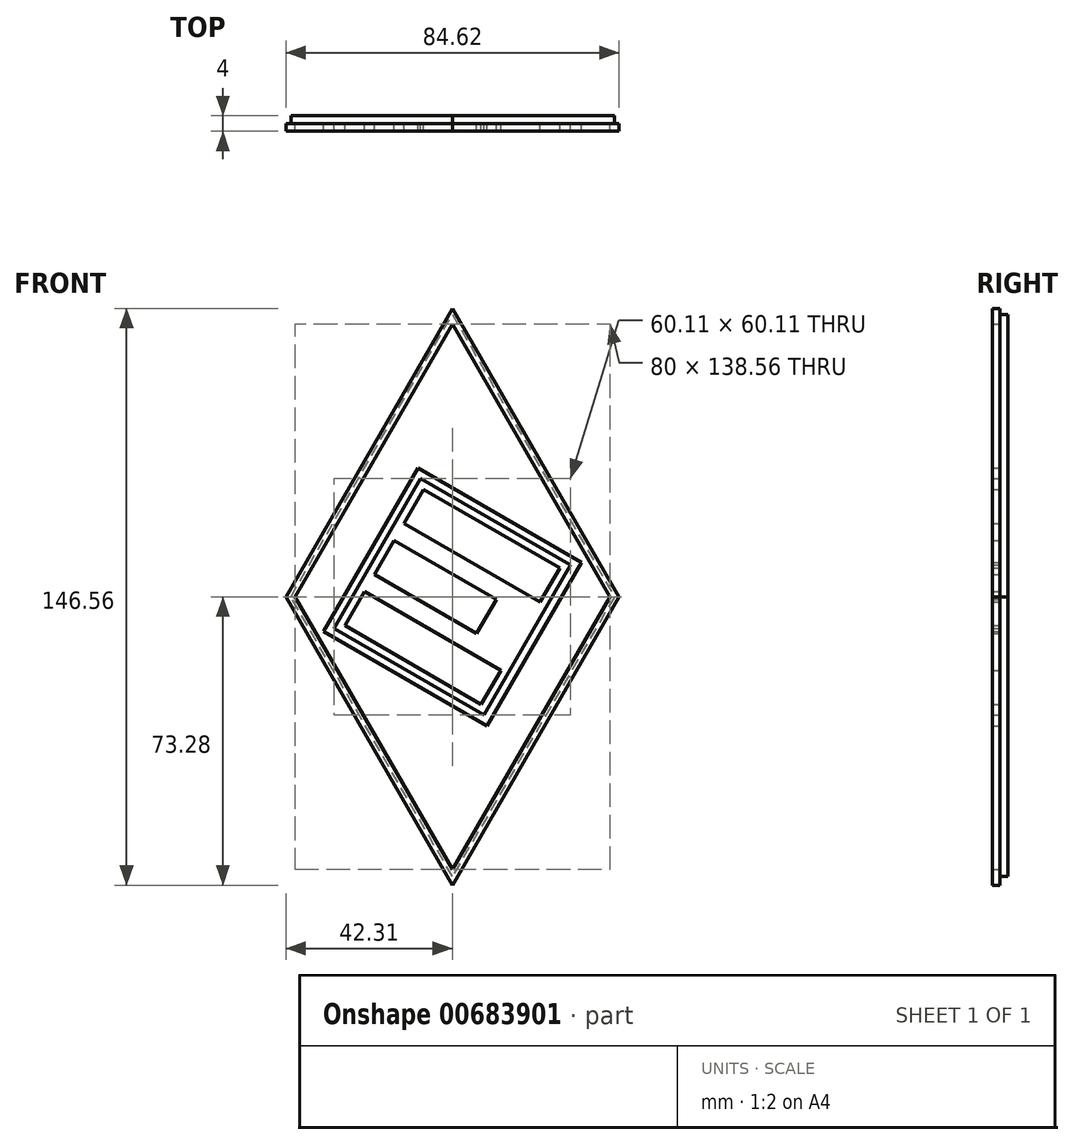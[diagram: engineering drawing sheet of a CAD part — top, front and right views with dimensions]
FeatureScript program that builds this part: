
annotation { "Feature Type Name" : "Feature", "Feature Type Description" : "" }
export const myFeature = defineFeature(function(context is Context, id is Id, definition is map)
    precondition{}
    {
        {
            var Q0;
            Q0=qCreatedBy(makeId("Front.planeOp"),FACE);
            var sketch = newSketch(context, id + "F0", { "sketchPlane" : qUnion([Q0])});
            skLineSegment(sketch, "E0.bottom", {"start": v(7.32, -27.32) * mm, "end": v(-27.32, -7.32) * mm});
            skLineSegment(sketch, "E0.top", {"start": v(12.32, -18.66) * mm, "end": v(-22.32, 1.34) * mm});
            skLineSegment(sketch, "E0.left", {"start": v(7.32, -27.32) * mm, "end": v(12.32, -18.66) * mm});
            skLineSegment(sketch, "E0.right", {"start": v(-27.32, -7.32) * mm, "end": v(-22.32, 1.34) * mm});
            skLineSegment(sketch, "E1.bottom", {"start": v(-14.82, 14.33) * mm, "end": v(11.16, -0.67) * mm});
            skLineSegment(sketch, "E1.top", {"start": v(-19.82, 5.67) * mm, "end": v(6.16, -9.33) * mm});
            skLineSegment(sketch, "E1.left", {"start": v(-14.82, 14.33) * mm, "end": v(-19.82, 5.67) * mm});
            skLineSegment(sketch, "E1.right", {"start": v(11.16, -0.67) * mm, "end": v(6.16, -9.33) * mm});
            skLineSegment(sketch, "E2.bottom", {"start": v(-12.32, 18.66) * mm, "end": v(22.32, -1.34) * mm});
            skLineSegment(sketch, "E2.top", {"start": v(-7.32, 27.32) * mm, "end": v(27.32, 7.32) * mm});
            skLineSegment(sketch, "E2.left", {"start": v(-12.32, 18.66) * mm, "end": v(-7.32, 27.32) * mm});
            skLineSegment(sketch, "E2.right", {"start": v(22.32, -1.34) * mm, "end": v(27.32, 7.32) * mm});
            skLineSegment(sketch, "E3.0", {"start": v(-22.32, 1.34) * mm, "end": v(-22.32, 1.34) * mm});
            skLineSegment(sketch, "E3.1", {"start": v(-22.32, 1.34) * mm, "end": v(-19.82, 5.67) * mm, "construction": true});
            skLineSegment(sketch, "E3.8", {"start": v(-14.82, 14.33) * mm, "end": v(-14.82, 14.33) * mm});
            skLineSegment(sketch, "E3.9", {"start": v(-14.82, 14.33) * mm, "end": v(-12.32, 18.66) * mm, "construction": true});
            skLineSegment(sketch, "E4.0", {"start": v(-22.32, 1.34) * mm, "end": v(-12.32, 18.66) * mm, "construction": true});
            skLineSegment(sketch, "E5.bottom", {"start": v(30.05, 8.05) * mm, "end": v(-8.05, 30.05) * mm});
            skLineSegment(sketch, "E5.top", {"start": v(8.05, -30.05) * mm, "end": v(-30.05, -8.05) * mm});
            skLineSegment(sketch, "E5.left", {"start": v(30.05, 8.05) * mm, "end": v(8.05, -30.05) * mm});
            skLineSegment(sketch, "E5.right", {"start": v(-8.05, 30.05) * mm, "end": v(-30.05, -8.05) * mm});
            skLineSegment(sketch, "E6", {"start": v(0, -69.28) * mm, "end": v(0, 69.28) * mm});
            skLineSegment(sketch, "E7", {"start": v(-40, 0) * mm, "end": v(40, 0) * mm});
            skLineSegment(sketch, "E8", {"start": v(0, 69.28) * mm, "end": v(40, 0) * mm});
            skLineSegment(sketch, "E9", {"start": v(0, -69.28) * mm, "end": v(40, 0) * mm});
            skLineSegment(sketch, "E10", {"start": v(-40, 0) * mm, "end": v(0, -69.28) * mm});
            skLineSegment(sketch, "E11", {"start": v(-40, 0) * mm, "end": v(0, 69.28) * mm});
            skPoint(sketch, "E12", {"position": v(-42.3, 0) * mm});
            skPoint(sketch, "E13", {"position": v(42.3, 0) * mm});
            skPoint(sketch, "E14", {"position": v(0, 73.28) * mm});
            skPoint(sketch, "E15", {"position": v(0, -73.28) * mm});
            skLineSegment(sketch, "E16", {"start": v(-42.3, 0) * mm, "end": v(0, 73.28) * mm});
            skLineSegment(sketch, "E17", {"start": v(0, 73.28) * mm, "end": v(42.3, 0) * mm});
            skLineSegment(sketch, "E18", {"start": v(0, -73.28) * mm, "end": v(42.3, 0) * mm});
            skLineSegment(sketch, "E19", {"start": v(0, -73.28) * mm, "end": v(-42.3, 0) * mm});
            skLineSegment(sketch, "E20", {"start": v(-8.78, 32.78) * mm, "end": v(32.78, 8.78) * mm});
            skLineSegment(sketch, "E21", {"start": v(32.78, 8.78) * mm, "end": v(8.78, -32.78) * mm});
            skLineSegment(sketch, "E22", {"start": v(8.78, -32.78) * mm, "end": v(-32.78, -8.78) * mm});
            skLineSegment(sketch, "E23", {"start": v(-32.78, -8.78) * mm, "end": v(-8.78, 32.78) * mm});
            skSolve(sketch);
        }
        {
            var Q0;
            Q0=makeQuery(id+"F0.imprint","IMPRINT",FACE,{"disambiguationData":[TD([[makeQuery(id+"F0.imprint","IMPRINT",EDGE,{"derivedFrom":sQuery(id+"F0.wireOp",EDGE,"E8")}),1.0]])]});
            var Q1;
            {var subQ1=sQuery(id+"F0.wireOp",EDGE,"E5.bottom");var subQ8=sQuery(id+"F0.wireOp",EDGE,"E5.right");var subQ11=makeQuery(id+"F0.imprint","INTERSECT",VERTEX,{"derivedFrom":[subQ1,subQ8]});Q1=makeQuery(id+"F0.imprint","IMPRINT",FACE,{"disambiguationData":[TD([[makeQuery(id+"F0.imprint","IMPRINT",EDGE,{"disambiguationData":[TD([[subQ11,1.0]])],"derivedFrom":subQ1}),-1.0]])]});}
            var Q2;
            {var subQ1=sQuery(id+"F0.wireOp",EDGE,"E5.bottom");var subQ5=sQuery(id+"F0.wireOp",EDGE,"E5.left");var subQ6=makeQuery(id+"F0.imprint","INTERSECT",VERTEX,{"derivedFrom":[subQ1,subQ5]});Q2=makeQuery(id+"F0.imprint","IMPRINT",FACE,{"disambiguationData":[TD([[makeQuery(id+"F0.imprint","IMPRINT",EDGE,{"disambiguationData":[TD([[subQ6,-1.0]])],"derivedFrom":subQ1}),-1.0]])]});}
            var Q3;
            {var subQ1=sQuery(id+"F0.wireOp",EDGE,"E5.top");var subQ6=sQuery(id+"F0.wireOp",EDGE,"E5.left");var subQ10=makeQuery(id+"F0.imprint","INTERSECT",VERTEX,{"derivedFrom":[subQ1,subQ6]});Q3=makeQuery(id+"F0.imprint","IMPRINT",FACE,{"disambiguationData":[TD([[makeQuery(id+"F0.imprint","IMPRINT",EDGE,{"disambiguationData":[TD([[subQ10,-1.0]])],"derivedFrom":subQ1}),1.0]])]});}
            var Q4;
            {var subQ1=sQuery(id+"F0.wireOp",EDGE,"E5.right");var subQ6=sQuery(id+"F0.wireOp",EDGE,"E5.top");var subQ10=makeQuery(id+"F0.imprint","INTERSECT",VERTEX,{"derivedFrom":[subQ6,subQ1]});Q4=makeQuery(id+"F0.imprint","IMPRINT",FACE,{"disambiguationData":[TD([[makeQuery(id+"F0.imprint","IMPRINT",EDGE,{"disambiguationData":[TD([[subQ10,1.0]])],"derivedFrom":subQ6}),1.0]])]});}
            var Q5;
            {var subQ0=sQuery(id+"F0.wireOp",EDGE,"E1.left");Q5=makeQuery(id+"F0.imprint","IMPRINT",FACE,{"disambiguationData":[TD([[makeQuery(id+"F0.imprint","IMPRINT",EDGE,{"derivedFrom":subQ0}),1.0]])]});}
            var Q6;
            {var subQ0=sQuery(id+"F0.wireOp",EDGE,"E7");var subQ1=sQuery(id+"F0.wireOp",EDGE,"E1.top");var subQ2=makeQuery(id+"F0.imprint","INTERSECT",VERTEX,{"derivedFrom":[subQ1,subQ0]});Q6=makeQuery(id+"F0.imprint","IMPRINT",FACE,{"disambiguationData":[TD([[makeQuery(id+"F0.imprint","IMPRINT",EDGE,{"disambiguationData":[TD([[subQ2,-1.0]])],"derivedFrom":subQ1}),1.0]])]});}
            var Q7;
            {var subQ5=sQuery(id+"F0.wireOp",EDGE,"E1.right");Q7=makeQuery(id+"F0.imprint","IMPRINT",FACE,{"disambiguationData":[TD([[makeQuery(id+"F0.imprint","IMPRINT",EDGE,{"derivedFrom":subQ5}),-1.0]])]});}
            var Q8;
            {var subQ0=sQuery(id+"F0.wireOp",EDGE,"E6");var subQ1=sQuery(id+"F0.wireOp",EDGE,"E1.bottom");var subQ2=makeQuery(id+"F0.imprint","INTERSECT",VERTEX,{"derivedFrom":[subQ1,subQ0]});Q8=makeQuery(id+"F0.imprint","IMPRINT",FACE,{"disambiguationData":[TD([[makeQuery(id+"F0.imprint","IMPRINT",EDGE,{"disambiguationData":[TD([[subQ2,-1.0]])],"derivedFrom":subQ1}),-1.0]])]});}
            var Q9;
            {var subQ5=sQuery(id+"F0.wireOp",EDGE,"E6");var subQ6=sQuery(id+"F0.wireOp",EDGE,"E2.bottom");var subQ7=makeQuery(id+"F0.imprint","INTERSECT",VERTEX,{"derivedFrom":[subQ6,subQ5]});Q9=makeQuery(id+"F0.imprint","IMPRINT",FACE,{"disambiguationData":[TD([[makeQuery(id+"F0.imprint","IMPRINT",EDGE,{"disambiguationData":[TD([[subQ7,-1.0]])],"derivedFrom":subQ6}),1.0]])]});}
            var Q10;
            {var subQ0=sQuery(id+"F0.wireOp",EDGE,"E2.left");Q10=makeQuery(id+"F0.imprint","IMPRINT",FACE,{"disambiguationData":[TD([[makeQuery(id+"F0.imprint","IMPRINT",EDGE,{"derivedFrom":subQ0}),-1.0]])]});}
            var Q11;
            {var subQ0=sQuery(id+"F0.wireOp",EDGE,"E2.right");var subQ1=sQuery(id+"F0.wireOp",EDGE,"E2.bottom");var subQ2=makeQuery(id+"F0.imprint","INTERSECT",VERTEX,{"derivedFrom":[subQ1,subQ0]});Q11=makeQuery(id+"F0.imprint","IMPRINT",FACE,{"disambiguationData":[TD([[makeQuery(id+"F0.imprint","IMPRINT",EDGE,{"disambiguationData":[TD([[subQ2,1.0]])],"derivedFrom":subQ1}),1.0]])]});}
            var Q12;
            {var subQ0=sQuery(id+"F0.wireOp",EDGE,"E0.left");Q12=makeQuery(id+"F0.imprint","IMPRINT",FACE,{"disambiguationData":[TD([[makeQuery(id+"F0.imprint","IMPRINT",EDGE,{"derivedFrom":subQ0}),1.0]])]});}
            var Q13;
            {var subQ1=sQuery(id+"F0.wireOp",EDGE,"E0.bottom");var subQ7=sQuery(id+"F0.wireOp",EDGE,"E0.right");var subQ9=makeQuery(id+"F0.imprint","INTERSECT",VERTEX,{"derivedFrom":[subQ1,subQ7]});Q13=makeQuery(id+"F0.imprint","IMPRINT",FACE,{"disambiguationData":[TD([[makeQuery(id+"F0.imprint","IMPRINT",EDGE,{"disambiguationData":[TD([[subQ9,1.0]])],"derivedFrom":subQ1}),-1.0]])]});}
            var Q14;
            {var subQ0=sQuery(id+"F0.wireOp",EDGE,"E0.right");var subQ1=sQuery(id+"F0.wireOp",EDGE,"E0.top");var subQ2=makeQuery(id+"F0.imprint","INTERSECT",VERTEX,{"derivedFrom":[subQ1,subQ0]});Q14=makeQuery(id+"F0.imprint","IMPRINT",FACE,{"disambiguationData":[TD([[makeQuery(id+"F0.imprint","IMPRINT",EDGE,{"disambiguationData":[TD([[subQ2,1.0]])],"derivedFrom":subQ1}),1.0]])]});}
            extrude(context, id + "F1", {"entities" : qUnion([Q0, Q1, Q2, Q3, Q4, Q5, Q6, Q7, Q8, Q9, Q10, Q11, Q12, Q13, Q14]), "depth" : 2 * mm, "offsetDistance" : 25 * mm});
        }
        {
            var Q0;
            Q0=qCreatedBy(makeId("Front.planeOp"),FACE);
            var sketch = newSketch(context, id + "F2", { "sketchPlane" : qUnion([Q0])});
            skLineSegment(sketch, "E24", {"start": v(-41.04, 0) * mm, "end": v(0, 71.79) * mm});
            skLineSegment(sketch, "E25", {"start": v(0, 71.79) * mm, "end": v(41.14, 0) * mm});
            skLineSegment(sketch, "E26", {"start": v(41.14, 0) * mm, "end": v(0, -71.05) * mm});
            skLineSegment(sketch, "E27", {"start": v(0, -71.05) * mm, "end": v(-41.04, 0) * mm});
            skSolve(sketch);
        }
        {
            var Q0;
            Q0=makeQuery(id+"F2.imprint","IMPRINT",FACE,{"disambiguationData":[TD([[makeQuery(id+"F2.imprint","IMPRINT",EDGE,{"derivedFrom":sQuery(id+"F2.wireOp",EDGE,"E24")}),-1.0]])]});
            extrude(context, id + "F3", {"entities" : qUnion([Q0]), "oppositeDirection" : true, "depth" : 2 * mm, "offsetDistance" : 25 * mm});
        }
    });
